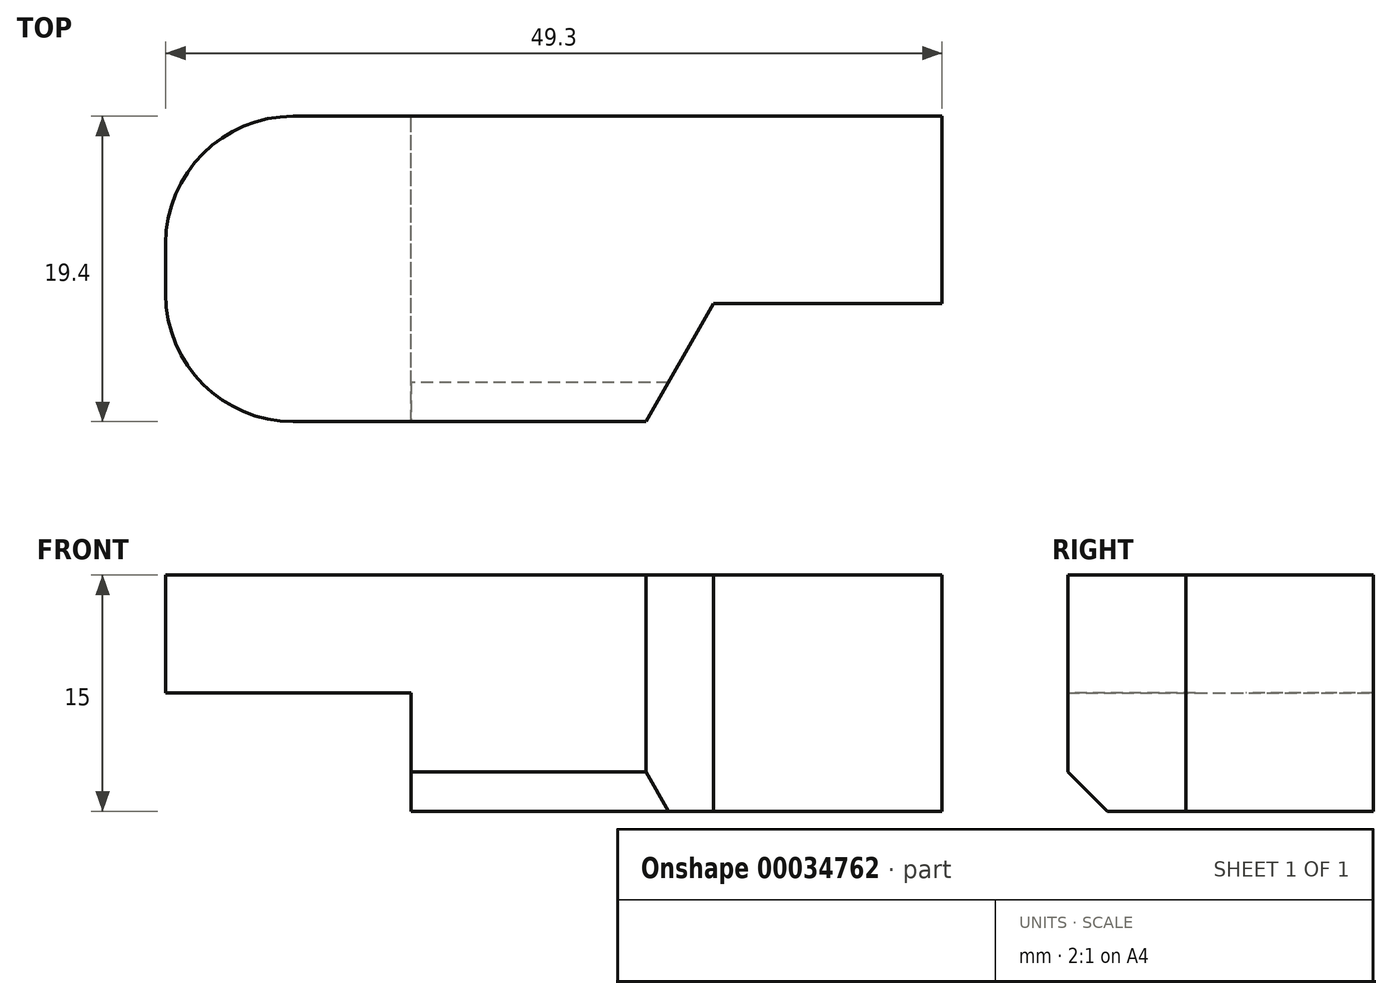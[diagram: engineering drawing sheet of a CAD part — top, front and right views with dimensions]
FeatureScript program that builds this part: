
annotation { "Feature Type Name" : "Feature", "Feature Type Description" : "" }
export const myFeature = defineFeature(function(context is Context, id is Id, definition is map)
    precondition{}
    {
        {
            var Q0;
            Q0=qCreatedBy(makeId("Front.planeOp"),FACE);
            var sketch = newSketch(context, id + "F0", { "sketchPlane" : qUnion([Q0])});
            skLineSegment(sketch, "E0", {"start": v(-34.8, 25.35) * mm, "end": v(-34.8, 17.85) * mm});
            skLineSegment(sketch, "E1", {"start": v(-34.8, 17.85) * mm, "end": v(-19.2, 17.85) * mm});
            skLineSegment(sketch, "E2", {"start": v(-19.2, 17.85) * mm, "end": v(-19.2, 13.12) * mm});
            skLineSegment(sketch, "E3", {"start": v(-19.2, 13.12) * mm, "end": v(-19.2, 10.35) * mm});
            skLineSegment(sketch, "E4", {"start": v(-19.2, 10.35) * mm, "end": v(0, 10.35) * mm});
            skLineSegment(sketch, "E5", {"start": v(0, 10.35) * mm, "end": v(0, 25.35) * mm});
            skLineSegment(sketch, "E6", {"start": v(0, 25.35) * mm, "end": v(-34.8, 25.35) * mm});
            skLineSegment(sketch, "E7", {"start": v(0, 10.35) * mm, "end": v(14.5, 10.35) * mm});
            skLineSegment(sketch, "E8", {"start": v(14.5, 10.35) * mm, "end": v(14.5, 25.35) * mm});
            skLineSegment(sketch, "E9", {"start": v(14.5, 25.35) * mm, "end": v(0, 25.35) * mm});
            skSolve(sketch);
        }
        {
            var Q0;
            Q0=makeQuery(id+"F0.imprint","IMPRINT",FACE,{"disambiguationData":[TD([[makeQuery(id+"F0.imprint","IMPRINT",EDGE,{"derivedFrom":sQuery(id+"F0.wireOp",EDGE,"E5")}),-1.0]])]});
            var Q1;
            Q1=makeQuery(id+"F0.imprint","IMPRINT",FACE,{"disambiguationData":[TD([[makeQuery(id+"F0.imprint","IMPRINT",EDGE,{"derivedFrom":sQuery(id+"F0.wireOp",EDGE,"E0")}),1.0]])]});
            extrude(context, id + "F1", {"entities" : qUnion([Q0, Q1]), "depth" : 19.4 * mm});
        }
        {
            var Q0;
            Q0=makeQuery(id+"F1.opExtrude","CAP_EDGE",EDGE,{"disambiguationData":[OSD([sQuery(id+"F0.wireOp",EDGE,"E0")])],"isStart":true});
            fillet(context, id + "F2", {"entities" : qUnion([Q0]), "radius" : 8.1 * mm, "tangentPropagation" : true, "allowEdgeOverflow" : false});
        }
        {
            var Q0;
            Q0=makeQuery(id+"F1.opExtrude","CAP_EDGE",EDGE,{"disambiguationData":[OSD([sQuery(id+"F0.wireOp",EDGE,"E0")])],"isStart":false});
            fillet(context, id + "F3", {"entities" : qUnion([Q0]), "radius" : 8.1 * mm, "tangentPropagation" : true, "allowEdgeOverflow" : false});
        }
        {
            var Q0;
            Q0=makeQuery(id+"F1.opExtrude","CAP_EDGE",EDGE,{"disambiguationData":[OSD([sQuery(id+"F0.wireOp",EDGE,"E4"),sQuery(id+"F0.wireOp",EDGE,"E7")])],"isStart":false});
            chamfer(context, id + "F4", {"entities" : qUnion([Q0]), "width" : 2.5 * mm, "tangentPropagation" : true});
        }
        {
            var Q0;
            Q0=makeQuery(id+"F1.opExtrude","SWEPT_FACE",FACE,{"disambiguationData":[OSD([sQuery(id+"F0.wireOp",EDGE,"E4"),sQuery(id+"F0.wireOp",EDGE,"E7")])]});
            var sketch = newSketch(context, id + "F5", { "sketchPlane" : qUnion([Q0])});
            skLineSegment(sketch, "E10", {"start": v(14.5, 11.9) * mm, "end": v(0, 11.9) * mm});
            skLineSegment(sketch, "E11", {"start": v(0, 11.9) * mm, "end": v(-4.3, 19.4) * mm});
            skLineSegment(sketch, "E12", {"start": v(-4.3, 19.4) * mm, "end": v(14.5, 19.4) * mm});
            skLineSegment(sketch, "E13", {"start": v(14.5, 19.4) * mm, "end": v(14.5, 11.9) * mm});
            skSolve(sketch);
        }
        {
            var Q0;
            Q0 = qSketchRegion(id + "F5", true);
            extrude(context, id + "F6", {"entities" : qUnion([Q0]), "operationType" : NewBodyOperationType.REMOVE, "endBound" : BoundingType.THROUGH_ALL, "oppositeDirection" : true, "depth" : 25 * mm});
        }
    });
